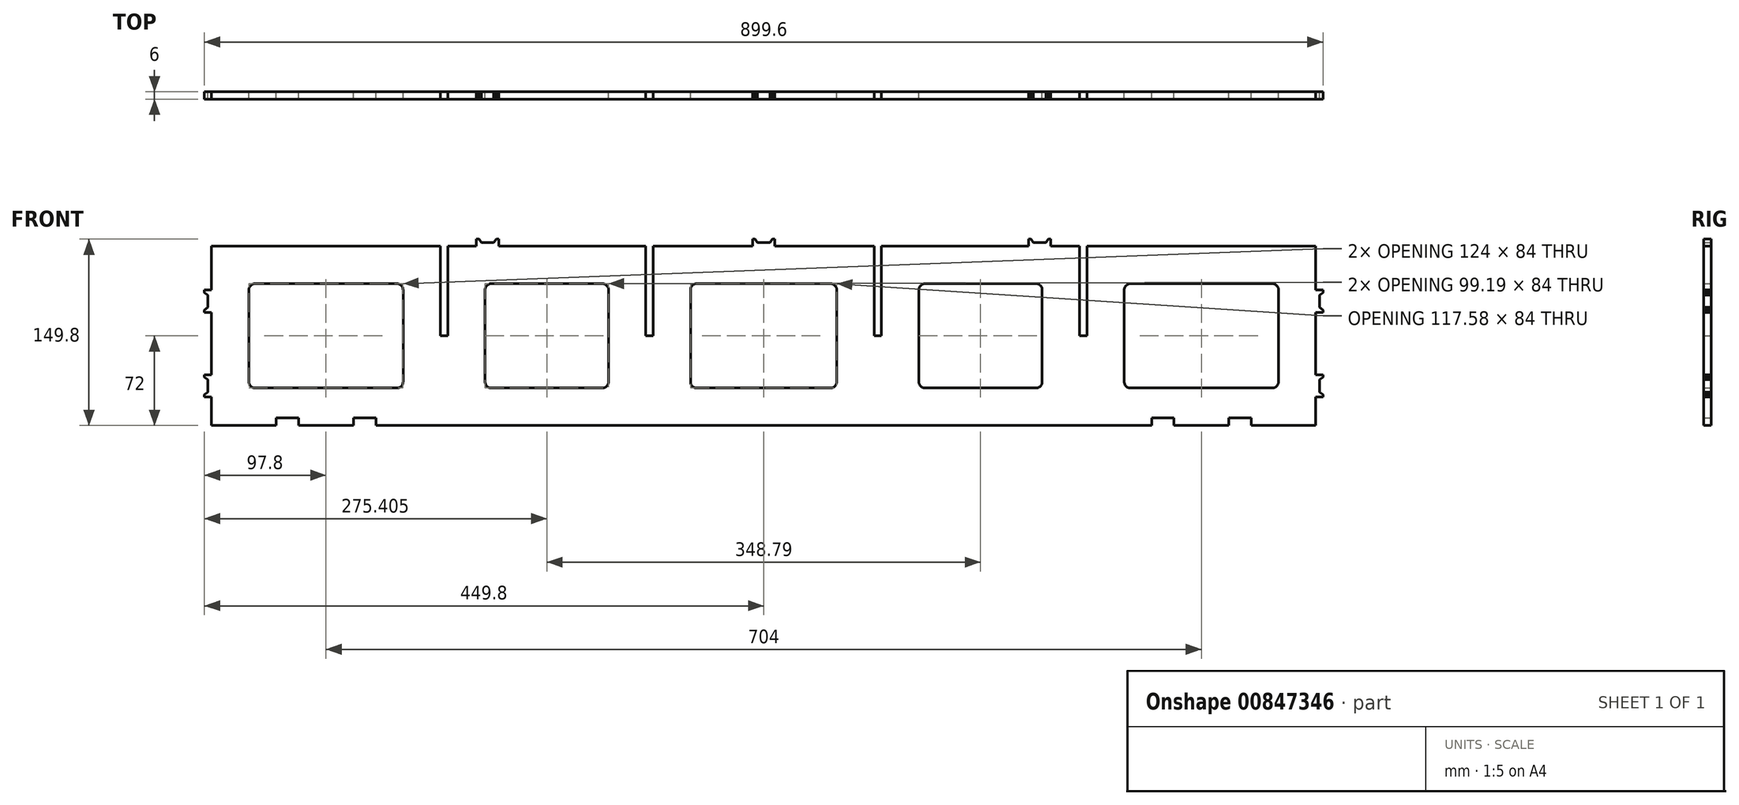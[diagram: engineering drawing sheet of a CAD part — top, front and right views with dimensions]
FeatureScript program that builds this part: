
annotation { "Feature Type Name" : "Feature", "Feature Type Description" : "" }
export const myFeature = defineFeature(function(context is Context, id is Id, definition is map)
    precondition{}
    {
        {
            var Q0;
            Q0=qCreatedBy(makeId("Front.planeOp"),FACE);
            var sketch = newSketch(context, id + "F0", { "sketchPlane" : qUnion([Q0])});
            skLineSegment(sketch, "E0.bottom", {"start": v(0, 0) * mm, "end": v(184, 0) * mm});
            skLineSegment(sketch, "E0.top", {"start": v(0, -144) * mm, "end": v(52, -144) * mm});
            skLineSegment(sketch, "E0.left", {"start": v(0, 0) * mm, "end": v(0, -35.2) * mm});
            skLineSegment(sketch, "E0.right", {"start": v(888, 0) * mm, "end": v(888, -35.2) * mm});
            skLineSegment(sketch, "E1", {"start": v(213, 0) * mm, "end": v(213, 5.8) * mm});
            skLineSegment(sketch, "E2", {"start": v(213, 5.8) * mm, "end": v(215, 5.8) * mm});
            skLineSegment(sketch, "E3", {"start": v(215, 5.8) * mm, "end": v(217, 3) * mm});
            skLineSegment(sketch, "E4", {"start": v(217, 3) * mm, "end": v(227, 3) * mm});
            skLineSegment(sketch, "E5", {"start": v(227, 3) * mm, "end": v(229, 5.8) * mm});
            skLineSegment(sketch, "E6", {"start": v(229, 5.8) * mm, "end": v(231, 5.8) * mm});
            skLineSegment(sketch, "E7", {"start": v(231, 5.8) * mm, "end": v(231, 0) * mm});
            skLineSegment(sketch, "E8.trimOffspring", {"start": v(231, 0) * mm, "end": v(349.2, 0) * mm});
            skLineSegment(sketch, "E9", {"start": v(435, 0) * mm, "end": v(435, 5.8) * mm});
            skLineSegment(sketch, "E10", {"start": v(435, 5.8) * mm, "end": v(437, 5.8) * mm});
            skLineSegment(sketch, "E11", {"start": v(437, 5.8) * mm, "end": v(439, 3) * mm});
            skLineSegment(sketch, "E12", {"start": v(439, 3) * mm, "end": v(449, 3) * mm});
            skLineSegment(sketch, "E13", {"start": v(449, 3) * mm, "end": v(451, 5.8) * mm});
            skLineSegment(sketch, "E14", {"start": v(451, 5.8) * mm, "end": v(453, 5.8) * mm});
            skLineSegment(sketch, "E15", {"start": v(453, 5.8) * mm, "end": v(453, 0) * mm});
            skLineSegment(sketch, "E16.trimOffspring", {"start": v(453, 0) * mm, "end": v(532.8, 0) * mm});
            skLineSegment(sketch, "E17", {"start": v(657, 0) * mm, "end": v(657, 5.8) * mm});
            skLineSegment(sketch, "E18", {"start": v(657, 5.8) * mm, "end": v(659, 5.8) * mm});
            skLineSegment(sketch, "E19", {"start": v(659, 5.8) * mm, "end": v(661, 3) * mm});
            skLineSegment(sketch, "E20", {"start": v(661, 3) * mm, "end": v(671, 3) * mm});
            skLineSegment(sketch, "E21", {"start": v(671, 3) * mm, "end": v(673, 5.8) * mm});
            skLineSegment(sketch, "E22", {"start": v(673, 5.8) * mm, "end": v(675, 5.8) * mm});
            skLineSegment(sketch, "E23", {"start": v(675, 5.8) * mm, "end": v(675, 0) * mm});
            skLineSegment(sketch, "E24", {"start": v(0, -35.2) * mm, "end": v(-5.8, -35.2) * mm});
            skLineSegment(sketch, "E25", {"start": v(-5.8, -35.2) * mm, "end": v(-5.8, -37.2) * mm});
            skLineSegment(sketch, "E26", {"start": v(-5.8, -37.2) * mm, "end": v(-3, -39.2) * mm});
            skLineSegment(sketch, "E27", {"start": v(-3, -39.2) * mm, "end": v(-3, -49.2) * mm});
            skLineSegment(sketch, "E28", {"start": v(-3, -49.2) * mm, "end": v(-5.8, -51.21) * mm});
            skLineSegment(sketch, "E29", {"start": v(-5.8, -51.21) * mm, "end": v(-5.8, -53.21) * mm});
            skLineSegment(sketch, "E30", {"start": v(-5.8, -53.21) * mm, "end": v(0, -53.21) * mm});
            skLineSegment(sketch, "E31", {"start": v(0, -103.23) * mm, "end": v(-5.8, -103.23) * mm});
            skLineSegment(sketch, "E32", {"start": v(-5.8, -103.23) * mm, "end": v(-5.8, -105.23) * mm});
            skLineSegment(sketch, "E33", {"start": v(-5.8, -105.23) * mm, "end": v(-3, -107.23) * mm});
            skLineSegment(sketch, "E34", {"start": v(-3, -107.23) * mm, "end": v(-3, -117.23) * mm});
            skLineSegment(sketch, "E35", {"start": v(-3, -117.23) * mm, "end": v(-5.8, -119.23) * mm});
            skLineSegment(sketch, "E36", {"start": v(-5.8, -119.23) * mm, "end": v(-5.8, -121.23) * mm});
            skLineSegment(sketch, "E37", {"start": v(-5.8, -121.23) * mm, "end": v(0, -121.23) * mm});
            skLineSegment(sketch, "E38.trimOffspring", {"start": v(0, -53.21) * mm, "end": v(0, -103.23) * mm});
            skLineSegment(sketch, "E39", {"start": v(888, -35.2) * mm, "end": v(893.8, -35.2) * mm});
            skLineSegment(sketch, "E40", {"start": v(893.8, -35.2) * mm, "end": v(893.8, -37.2) * mm});
            skLineSegment(sketch, "E41", {"start": v(893.8, -37.21) * mm, "end": v(891, -39.2) * mm});
            skLineSegment(sketch, "E42", {"start": v(891, -39.2) * mm, "end": v(891, -49.2) * mm});
            skLineSegment(sketch, "E43", {"start": v(891, -49.2) * mm, "end": v(893.8, -51.2) * mm});
            skLineSegment(sketch, "E44", {"start": v(893.8, -51.2) * mm, "end": v(893.8, -53.2) * mm});
            skLineSegment(sketch, "E45", {"start": v(893.8, -53.2) * mm, "end": v(888, -53.2) * mm});
            skLineSegment(sketch, "E46.trimOffspring", {"start": v(888, -53.2) * mm, "end": v(888, -103.23) * mm});
            skLineSegment(sketch, "E47", {"start": v(888, -103.23) * mm, "end": v(893.8, -103.23) * mm});
            skLineSegment(sketch, "E48", {"start": v(893.8, -103.23) * mm, "end": v(893.8, -105.23) * mm});
            skLineSegment(sketch, "E49", {"start": v(893.8, -105.23) * mm, "end": v(891, -107.23) * mm});
            skLineSegment(sketch, "E50", {"start": v(891, -107.23) * mm, "end": v(891, -117.23) * mm});
            skLineSegment(sketch, "E51", {"start": v(891, -117.23) * mm, "end": v(893.8, -119.23) * mm});
            skLineSegment(sketch, "E52", {"start": v(893.8, -119.23) * mm, "end": v(893.8, -121.23) * mm});
            skLineSegment(sketch, "E53", {"start": v(893.8, -121.23) * mm, "end": v(888, -121.23) * mm});
            skLineSegment(sketch, "E54", {"start": v(675, 0) * mm, "end": v(697.99, 0) * mm});
            skLineSegment(sketch, "E55", {"start": v(184, 0) * mm, "end": v(184, -72.01) * mm});
            skLineSegment(sketch, "E56", {"start": v(184, -72.01) * mm, "end": v(190, -72.01) * mm});
            skLineSegment(sketch, "E57", {"start": v(190, -72.01) * mm, "end": v(190, 0) * mm});
            skLineSegment(sketch, "E58.trimOffspring", {"start": v(190, 0) * mm, "end": v(213, 0) * mm});
            skLineSegment(sketch, "E59", {"start": v(349.2, 0) * mm, "end": v(349.2, -72) * mm});
            skLineSegment(sketch, "E60", {"start": v(349.2, -72) * mm, "end": v(355.2, -72) * mm});
            skLineSegment(sketch, "E61", {"start": v(355.2, -72) * mm, "end": v(355.2, 0) * mm});
            skLineSegment(sketch, "E62.trimOffspring", {"start": v(355.2, 0) * mm, "end": v(435, 0) * mm});
            skLineSegment(sketch, "E63", {"start": v(532.8, 0) * mm, "end": v(532.8, -72) * mm});
            skLineSegment(sketch, "E64", {"start": v(532.8, -72) * mm, "end": v(538.8, -72) * mm});
            skLineSegment(sketch, "E65", {"start": v(538.8, -72) * mm, "end": v(538.8, 0) * mm});
            skLineSegment(sketch, "E66.trimOffspring", {"start": v(538.8, 0) * mm, "end": v(657, 0) * mm});
            skLineSegment(sketch, "E67", {"start": v(697.99, 0) * mm, "end": v(697.99, -72) * mm});
            skLineSegment(sketch, "E68", {"start": v(697.99, -72) * mm, "end": v(704, -72) * mm});
            skLineSegment(sketch, "E69", {"start": v(704, -72) * mm, "end": v(704, 0) * mm});
            skLineSegment(sketch, "E70.trimOffspring", {"start": v(704, 0) * mm, "end": v(888, 0) * mm});
            skLineSegment(sketch, "E71.trimOffspring", {"start": v(0, -121.23) * mm, "end": v(0, -144) * mm});
            skLineSegment(sketch, "E72.trimOffspring", {"start": v(888, -121.23) * mm, "end": v(888, -144) * mm});
            skLineSegment(sketch, "E73", {"start": v(35, -30) * mm, "end": v(149, -30) * mm});
            skLineSegment(sketch, "E74", {"start": v(154, -35) * mm, "end": v(154, -109) * mm});
            skLineSegment(sketch, "E75", {"start": v(149, -114) * mm, "end": v(35, -114) * mm});
            skLineSegment(sketch, "E76", {"start": v(30, -109) * mm, "end": v(30, -35) * mm});
            skLineSegment(sketch, "E77", {"start": v(220, -35) * mm, "end": v(220, -109) * mm});
            skPoint(sketch, "E77.startSnap0", {"position": v(92, -30) * mm});
            skLineSegment(sketch, "E78", {"start": v(225, -114) * mm, "end": v(314.2, -114) * mm});
            skLineSegment(sketch, "E79", {"start": v(319.2, -109) * mm, "end": v(319.2, -35) * mm});
            skLineSegment(sketch, "E80", {"start": v(314.2, -30) * mm, "end": v(225, -30) * mm});
            skLineSegment(sketch, "E81", {"start": v(390.2, -30) * mm, "end": v(497.79, -30) * mm});
            skPoint(sketch, "E81.startSnap0", {"position": v(269.6, -30) * mm});
            skLineSegment(sketch, "E82", {"start": v(502.79, -35) * mm, "end": v(502.79, -109) * mm});
            skLineSegment(sketch, "E83", {"start": v(497.79, -114) * mm, "end": v(390.2, -114) * mm});
            skLineSegment(sketch, "E84", {"start": v(385.2, -109) * mm, "end": v(385.2, -35) * mm});
            skLineSegment(sketch, "E85", {"start": v(573.8, -30) * mm, "end": v(662.99, -30) * mm});
            skLineSegment(sketch, "E86", {"start": v(667.99, -35) * mm, "end": v(667.99, -109) * mm});
            skLineSegment(sketch, "E87", {"start": v(662.99, -114) * mm, "end": v(573.8, -114) * mm});
            skLineSegment(sketch, "E88", {"start": v(568.8, -109) * mm, "end": v(568.8, -35) * mm});
            skLineSegment(sketch, "E89", {"start": v(739, -30) * mm, "end": v(853, -30) * mm});
            skLineSegment(sketch, "E90", {"start": v(858, -35) * mm, "end": v(858, -109) * mm});
            skLineSegment(sketch, "E91", {"start": v(853, -114) * mm, "end": v(739, -114) * mm});
            skLineSegment(sketch, "E92", {"start": v(734, -109) * mm, "end": v(734, -35) * mm});
            skPoint(sketch, "E93.visualSharp", {"position": v(30, -30) * mm});
            skArc(sketch, "E93.filletArc", {"start": v(35, -30) * mm, "mid": v(31.46, -31.46) * mm, "end": v(30, -35) * mm});
            skPoint(sketch, "E94.visualSharp", {"position": v(154, -30) * mm});
            skArc(sketch, "E94.filletArc", {"start": v(154, -35) * mm, "mid": v(152.54, -31.46) * mm, "end": v(149, -30) * mm});
            skPoint(sketch, "E95.visualSharp", {"position": v(154, -114) * mm});
            skArc(sketch, "E95.filletArc", {"start": v(149, -114) * mm, "mid": v(152.54, -112.54) * mm, "end": v(154, -109) * mm});
            skPoint(sketch, "E96.visualSharp", {"position": v(30, -114) * mm});
            skArc(sketch, "E96.filletArc", {"start": v(30, -109) * mm, "mid": v(31.46, -112.54) * mm, "end": v(35, -114) * mm});
            skPoint(sketch, "E97.visualSharp", {"position": v(220, -30) * mm});
            skArc(sketch, "E97.filletArc", {"start": v(225, -30) * mm, "mid": v(221.47, -31.46) * mm, "end": v(220, -35) * mm});
            skPoint(sketch, "E98.visualSharp", {"position": v(319.2, -30) * mm});
            skArc(sketch, "E98.filletArc", {"start": v(319.2, -35) * mm, "mid": v(317.74, -31.46) * mm, "end": v(314.2, -30) * mm});
            skPoint(sketch, "E99.visualSharp", {"position": v(319.2, -114) * mm});
            skArc(sketch, "E99.filletArc", {"start": v(314.2, -114) * mm, "mid": v(317.74, -112.54) * mm, "end": v(319.2, -109) * mm});
            skPoint(sketch, "E100.visualSharp", {"position": v(220, -114) * mm});
            skArc(sketch, "E100.filletArc", {"start": v(220, -109) * mm, "mid": v(221.47, -112.54) * mm, "end": v(225, -114) * mm});
            skPoint(sketch, "E101.visualSharp", {"position": v(385.2, -114) * mm});
            skArc(sketch, "E101.filletArc", {"start": v(385.2, -109) * mm, "mid": v(386.67, -112.54) * mm, "end": v(390.2, -114) * mm});
            skPoint(sketch, "E102.visualSharp", {"position": v(385.2, -30) * mm});
            skArc(sketch, "E102.filletArc", {"start": v(390.2, -30) * mm, "mid": v(386.67, -31.46) * mm, "end": v(385.2, -35) * mm});
            skPoint(sketch, "E103.visualSharp", {"position": v(502.79, -30) * mm});
            skArc(sketch, "E103.filletArc", {"start": v(502.79, -35) * mm, "mid": v(501.33, -31.46) * mm, "end": v(497.79, -30) * mm});
            skPoint(sketch, "E104.visualSharp", {"position": v(502.79, -114) * mm});
            skArc(sketch, "E104.filletArc", {"start": v(497.79, -114) * mm, "mid": v(501.33, -112.54) * mm, "end": v(502.79, -109) * mm});
            skPoint(sketch, "E105.visualSharp", {"position": v(568.8, -114) * mm});
            skArc(sketch, "E105.filletArc", {"start": v(568.8, -109) * mm, "mid": v(570.26, -112.54) * mm, "end": v(573.8, -114) * mm});
            skPoint(sketch, "E106.visualSharp", {"position": v(568.8, -30) * mm});
            skArc(sketch, "E106.filletArc", {"start": v(573.8, -30) * mm, "mid": v(570.26, -31.46) * mm, "end": v(568.8, -35) * mm});
            skPoint(sketch, "E107.visualSharp", {"position": v(667.99, -30) * mm});
            skArc(sketch, "E107.filletArc", {"start": v(667.99, -35) * mm, "mid": v(666.53, -31.46) * mm, "end": v(662.99, -30) * mm});
            skPoint(sketch, "E108.visualSharp", {"position": v(667.99, -114) * mm});
            skArc(sketch, "E108.filletArc", {"start": v(662.99, -114) * mm, "mid": v(666.53, -112.54) * mm, "end": v(667.99, -109) * mm});
            skPoint(sketch, "E109.visualSharp", {"position": v(734, -114) * mm});
            skArc(sketch, "E109.filletArc", {"start": v(734, -109) * mm, "mid": v(735.46, -112.54) * mm, "end": v(739, -114) * mm});
            skPoint(sketch, "E110.visualSharp", {"position": v(734, -30) * mm});
            skArc(sketch, "E110.filletArc", {"start": v(739, -30) * mm, "mid": v(735.46, -31.46) * mm, "end": v(734, -35) * mm});
            skPoint(sketch, "E111.visualSharp", {"position": v(858, -30) * mm});
            skArc(sketch, "E111.filletArc", {"start": v(858, -35) * mm, "mid": v(856.54, -31.46) * mm, "end": v(853, -30) * mm});
            skPoint(sketch, "E112.visualSharp", {"position": v(858, -114) * mm});
            skArc(sketch, "E112.filletArc", {"start": v(853, -114) * mm, "mid": v(856.54, -112.54) * mm, "end": v(858, -109) * mm});
            skLineSegment(sketch, "E113", {"start": v(52, -144) * mm, "end": v(52, -138) * mm});
            skLineSegment(sketch, "E114", {"start": v(52, -138) * mm, "end": v(70.1, -138) * mm});
            skLineSegment(sketch, "E115", {"start": v(70.1, -138) * mm, "end": v(70.1, -144) * mm});
            skLineSegment(sketch, "E116", {"start": v(114, -144) * mm, "end": v(114, -138) * mm});
            skLineSegment(sketch, "E117", {"start": v(114, -138) * mm, "end": v(132.1, -138) * mm});
            skLineSegment(sketch, "E118", {"start": v(132.1, -138) * mm, "end": v(132.1, -144) * mm});
            skLineSegment(sketch, "E119.trimOffspring", {"start": v(70.1, -144) * mm, "end": v(114, -144) * mm});
            skLineSegment(sketch, "E120.trimOffspring", {"start": v(132.1, -144) * mm, "end": v(755.98, -144) * mm});
            skLineSegment(sketch, "E121", {"start": v(755.98, -144) * mm, "end": v(755.98, -138) * mm});
            skLineSegment(sketch, "E122", {"start": v(755.98, -138) * mm, "end": v(774, -138) * mm});
            skLineSegment(sketch, "E123", {"start": v(774, -138) * mm, "end": v(774, -144) * mm});
            skLineSegment(sketch, "E124", {"start": v(817.9, -144) * mm, "end": v(817.9, -138) * mm});
            skLineSegment(sketch, "E125", {"start": v(817.9, -138) * mm, "end": v(836, -138) * mm});
            skLineSegment(sketch, "E126", {"start": v(836, -138) * mm, "end": v(836, -144) * mm});
            skLineSegment(sketch, "E127.trimOffspring", {"start": v(774, -144) * mm, "end": v(817.9, -144) * mm});
            skLineSegment(sketch, "E128.trimOffspring", {"start": v(836, -144) * mm, "end": v(888, -144) * mm});
            skSolve(sketch);
        }
        {
            var Q0;
            Q0=makeQuery(id+"F0.imprint","IMPRINT",FACE,{"disambiguationData":[TD([[makeQuery(id+"F0.imprint","IMPRINT",EDGE,{"derivedFrom":sQuery(id+"F0.wireOp",EDGE,"E0.bottom")}),-1.0]])]});
            extrude(context, id + "F1", {"entities" : qUnion([Q0]), "depth" : 6 * mm, "offsetDistance" : 25 * mm});
        }
    });
